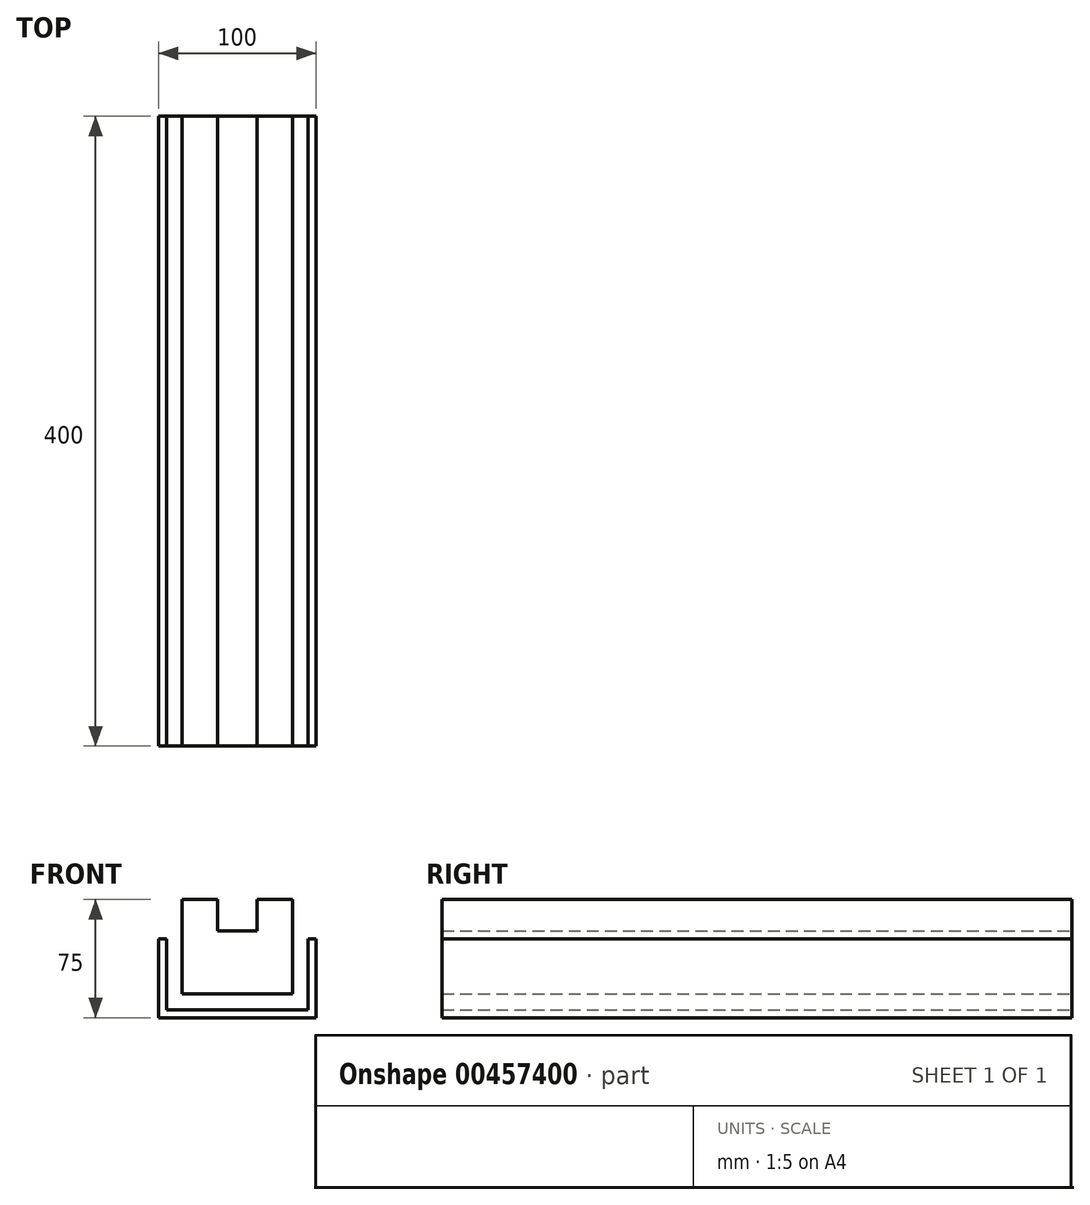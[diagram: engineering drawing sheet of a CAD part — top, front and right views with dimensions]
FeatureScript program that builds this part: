
annotation { "Feature Type Name" : "Feature", "Feature Type Description" : "" }
export const myFeature = defineFeature(function(context is Context, id is Id, definition is map)
    precondition{}
    {
        {
            var Q0;
            Q0=qCreatedBy(makeId("Front.planeOp"),FACE);
            var sketch = newSketch(context, id + "F0", { "sketchPlane" : qUnion([Q0])});
            skLineSegment(sketch, "E0", {"start": v(0, 0) * mm, "end": v(10, 0) * mm, "construction": true});
            skLineSegment(sketch, "E1.bottom", {"start": v(60, 25) * mm, "end": v(55, 25) * mm});
            skLineSegment(sketch, "E1.top", {"start": v(60, -25) * mm, "end": v(-40, -25) * mm});
            skLineSegment(sketch, "E1.left", {"start": v(60, 25) * mm, "end": v(60, -25) * mm});
            skLineSegment(sketch, "E1.right", {"start": v(-40, 25) * mm, "end": v(-40, -25) * mm});
            skPoint(sketch, "E1.middle", {"position": v(10, 0) * mm});
            skLineSegment(sketch, "E2.0", {"start": v(-35, 25) * mm, "end": v(-35, -20) * mm});
            skLineSegment(sketch, "E2.1", {"start": v(55, -20) * mm, "end": v(-35, -20) * mm});
            skLineSegment(sketch, "E2.2", {"start": v(55, 25) * mm, "end": v(55, -20) * mm});
            skLineSegment(sketch, "E3.trimOffspring", {"start": v(-35, 25) * mm, "end": v(-40, 25) * mm});
            skLineSegment(sketch, "E4.0", {"start": v(-25, 25) * mm, "end": v(-25, -10) * mm});
            skLineSegment(sketch, "E4.1", {"start": v(45, -10) * mm, "end": v(-25, -10) * mm});
            skLineSegment(sketch, "E4.2", {"start": v(45, 25) * mm, "end": v(45, -10) * mm});
            skLineSegment(sketch, "E5", {"start": v(-25, 25) * mm, "end": v(-25, 50) * mm});
            skLineSegment(sketch, "E6", {"start": v(-25, 50) * mm, "end": v(-2.5, 50) * mm});
            skLineSegment(sketch, "E7", {"start": v(45, 50) * mm, "end": v(45, 25) * mm});
            skLineSegment(sketch, "E8.top", {"start": v(-2.5, 30) * mm, "end": v(22.5, 30) * mm});
            skLineSegment(sketch, "E8.left", {"start": v(-2.5, 50) * mm, "end": v(-2.5, 30) * mm});
            skLineSegment(sketch, "E8.right", {"start": v(22.5, 50) * mm, "end": v(22.5, 30) * mm});
            skLineSegment(sketch, "E9.trimOffspring", {"start": v(22.5, 50) * mm, "end": v(45, 50) * mm});
            skSolve(sketch);
        }
        {
            var Q0;
            Q0=qSketchRegion(id+"F0",true);
            extrude(context, id + "F1", {"entities" : qUnion([Q0]), "endBound" : BoundingType.SYMMETRIC, "depth" : 400 * mm});
        }
    });
